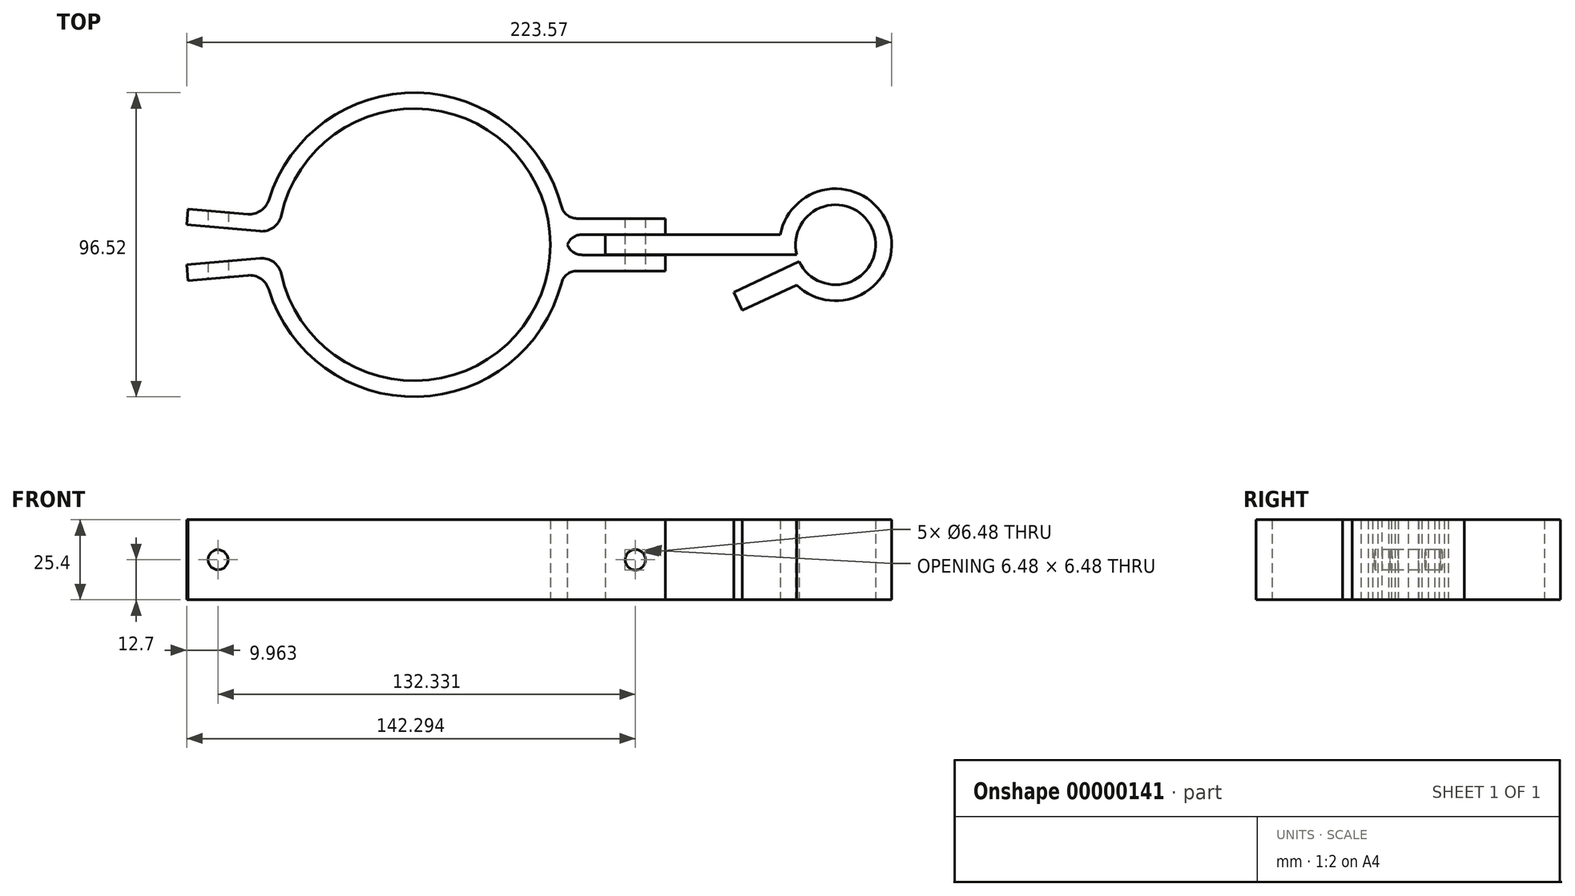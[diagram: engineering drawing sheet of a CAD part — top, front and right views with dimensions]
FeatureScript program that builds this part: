
annotation { "Feature Type Name" : "Feature", "Feature Type Description" : "" }
export const myFeature = defineFeature(function(context is Context, id is Id, definition is map)
    precondition{}
    {
        {
            var Q0;
            Q0=qCreatedBy(makeId("Top.planeOp"),FACE);
            var sketch = newSketch(context, id + "F0", { "sketchPlane" : qUnion([Q0])});
            skArc(sketch, "E0", {"start": v(-46.13, -14.18) * mm, "mid": v(48.26, 0) * mm, "end": v(-46.13, 14.18) * mm});
            skArc(sketch, "E1", {"start": v(-42.18, -9.25) * mm, "mid": v(43.18, 0) * mm, "end": v(-42.18, 9.25) * mm});
            skLineSegment(sketch, "E2", {"start": v(-52.75, 9.71) * mm, "end": v(-71.73, 11.38) * mm});
            skLineSegment(sketch, "E3", {"start": v(-71.73, 11.38) * mm, "end": v(-72.17, 6.31) * mm});
            skLineSegment(sketch, "E4", {"start": v(-72.17, 6.31) * mm, "end": v(-48.93, 4.28) * mm});
            skLineSegment(sketch, "E5", {"start": v(0, 0) * mm, "end": v(-48.26, 0) * mm, "construction": true});
            skLineSegment(sketch, "E6", {"start": v(0, 0) * mm, "end": v(0, 48.26) * mm, "construction": true});
            skLineSegment(sketch, "E7", {"start": v(47.54, 8.32) * mm, "end": v(79.65, 8.32) * mm});
            skLineSegment(sketch, "E8", {"start": v(79.65, 8.32) * mm, "end": v(79.65, 3.24) * mm});
            skLineSegment(sketch, "E9", {"start": v(79.65, 3.24) * mm, "end": v(48.15, 3.24) * mm});
            skLineSegment(sketch, "E10.0.MirrorCS", {"start": v(-72.17, -6.31) * mm, "end": v(-48.93, -4.28) * mm});
            skLineSegment(sketch, "E10.1.MirrorCS", {"start": v(-71.73, -11.38) * mm, "end": v(-72.17, -6.31) * mm});
            skLineSegment(sketch, "E10.2.MirrorCS", {"start": v(-52.75, -9.71) * mm, "end": v(-71.73, -11.38) * mm});
            skLineSegment(sketch, "E10.3.MirrorCS", {"start": v(79.65, -3.24) * mm, "end": v(48.15, -3.24) * mm});
            skLineSegment(sketch, "E10.4.MirrorCS", {"start": v(47.54, -8.32) * mm, "end": v(79.65, -8.32) * mm});
            skLineSegment(sketch, "E10.5.MirrorCS", {"start": v(79.65, -8.32) * mm, "end": v(79.65, -3.24) * mm});
            skPoint(sketch, "E11.visualSharp", {"position": v(-47.37, -9.24) * mm});
            skArc(sketch, "E11.filletArc", {"start": v(-46.13, -14.18) * mm, "mid": v(-48.65, -10.77) * mm, "end": v(-52.75, -9.71) * mm});
            skPoint(sketch, "E12.visualSharp", {"position": v(-47.37, 9.24) * mm});
            skArc(sketch, "E12.filletArc", {"start": v(-52.75, 9.71) * mm, "mid": v(-48.65, 10.77) * mm, "end": v(-46.13, 14.18) * mm});
            skPoint(sketch, "E13.visualSharp", {"position": v(-43.02, -3.76) * mm});
            skArc(sketch, "E13.filletArc", {"start": v(-42.18, -9.25) * mm, "mid": v(-44.62, -5.5) * mm, "end": v(-48.93, -4.28) * mm});
            skPoint(sketch, "E14.visualSharp", {"position": v(-43.02, 3.76) * mm});
            skArc(sketch, "E14.filletArc", {"start": v(-48.93, 4.28) * mm, "mid": v(-44.62, 5.5) * mm, "end": v(-42.18, 9.25) * mm});
            skSolve(sketch);
        }
        {
            var Q0;
            Q0=makeQuery(id+"F0.imprint","IMPRINT",FACE,{"disambiguationData":[TD([[makeQuery(id+"F0.imprint","IMPRINT",EDGE,{"derivedFrom":sQuery(id+"F0.wireOp",EDGE,"E1")}),-1.0]])]});
            var Q1;
            {var subQ1=sQuery(id+"F0.wireOp",EDGE,"E10.3.MirrorCS");Q1=makeQuery(id+"F0.imprint","IMPRINT",FACE,{"disambiguationData":[TD([[makeQuery(id+"F0.imprint","IMPRINT",EDGE,{"derivedFrom":subQ1}),1.0]])]});}
            var Q2;
            {var subQ1=sQuery(id+"F0.wireOp",EDGE,"E7");Q2=makeQuery(id+"F0.imprint","IMPRINT",FACE,{"disambiguationData":[TD([[makeQuery(id+"F0.imprint","IMPRINT",EDGE,{"derivedFrom":subQ1}),-1.0]])]});}
            extrude(context, id + "F1", {"entities" : qUnion([Q0, Q1, Q2]), "endBound" : BoundingType.SYMMETRIC, "depth" : 25.4 * mm});
        }
        {
            var Q0;
            Q0=qCreatedBy(makeId("Front.planeOp"),FACE);
            var sketch = newSketch(context, id + "F2", { "sketchPlane" : qUnion([Q0])});
            skCircle(sketch, "E15", {"center": v(-62.2, 0) * mm, "radius": 3.24 * mm});
            skCircle(sketch, "E16", {"center": v(70.12, 0) * mm, "radius": 3.24 * mm});
            skLineSegment(sketch, "E17", {"start": v(-62.2, 0) * mm, "end": v(-71.73, 0) * mm, "construction": true});
            skLineSegment(sketch, "E18", {"start": v(70.12, 0) * mm, "end": v(79.65, 0) * mm, "construction": true});
            skSolve(sketch);
        }
        {
            var Q0;
            Q0=makeQuery(id+"F1.opExtrude","SWEPT_EDGE",EDGE,{"disambiguationData":[OSD([sQuery(id+"F0.wireOp",EDGE,"E0"),sQuery(id+"F0.wireOp",EDGE,"E9")])]});
            var Q1;
            Q1=makeQuery(id+"F1.opExtrude","SWEPT_EDGE",EDGE,{"disambiguationData":[OSD([sQuery(id+"F0.wireOp",EDGE,"E0"),sQuery(id+"F0.wireOp",EDGE,"E10.3.MirrorCS")])]});
            var Q2;
            Q2=makeQuery(id+"F1.opExtrude","SWEPT_EDGE",EDGE,{"disambiguationData":[OSD([sQuery(id+"F0.wireOp",EDGE,"E0"),sQuery(id+"F0.wireOp",EDGE,"E7")])]});
            var Q3;
            Q3=makeQuery(id+"F1.opExtrude","SWEPT_EDGE",EDGE,{"disambiguationData":[OSD([sQuery(id+"F0.wireOp",EDGE,"E0"),sQuery(id+"F0.wireOp",EDGE,"E10.4.MirrorCS")])]});
            fillet(context, id + "F3", {"entities" : qUnion([Q0, Q1, Q2, Q3]), "radius" : 5.08 * mm, "tangentPropagation" : true, "allowEdgeOverflow" : false});
        }
        {
            var Q0;
            Q0=qCreatedBy(makeId("Top.planeOp"),FACE);
            var sketch = newSketch(context, id + "F4", { "sketchPlane" : qUnion([Q0])});
            skLineSegment(sketch, "E19.rect.bottom", {"start": v(60.6, -3.17) * mm, "end": v(121.33, -3.17) * mm});
            skLineSegment(sketch, "E19.rect.top", {"start": v(60.6, 3.18) * mm, "end": v(116.13, 3.18) * mm});
            skLineSegment(sketch, "E19.rect.left", {"start": v(60.6, -3.17) * mm, "end": v(60.6, 3.18) * mm});
            skPoint(sketch, "E19.rect.middle", {"position": v(90.96, 0) * mm});
            skArc(sketch, "E20", {"start": v(121.26, -12.77) * mm, "mid": v(150.55, 5.44) * mm, "end": v(116.13, 3.18) * mm});
            skArc(sketch, "E21", {"start": v(122.11, -5.37) * mm, "mid": v(145.58, 4.29) * mm, "end": v(121.33, -3.17) * mm});
            skLineSegment(sketch, "E22", {"start": v(122.11, -5.37) * mm, "end": v(101.3, -15.07) * mm});
            skLineSegment(sketch, "E23", {"start": v(101.3, -15.07) * mm, "end": v(104, -20.82) * mm});
            skLineSegment(sketch, "E24", {"start": v(104, -20.82) * mm, "end": v(121.26, -12.77) * mm});
            skPoint(sketch, "E25.orphan", {"position": v(121.33, 3.18) * mm});
            skSolve(sketch);
        }
        {
            var Q0;
            Q0=makeQuery(id+"F4.imprint","IMPRINT",FACE,{"disambiguationData":[TD([[makeQuery(id+"F4.imprint","IMPRINT",EDGE,{"derivedFrom":sQuery(id+"F4.wireOp",EDGE,"E19.rect.bottom")}),1.0]])]});
            extrude(context, id + "F5", {"entities" : qUnion([Q0]), "endBound" : BoundingType.SYMMETRIC, "depth" : 25.4 * mm});
        }
        {
            var Q0;
            {Q0=qUnion([makeQuery(id+"F2.imprint","IMPRINT",FACE,{"disambiguationData":[TD([[makeQuery(id+"F2.imprint","IMPRINT",EDGE,{"derivedFrom":sQuery(id+"F2.wireOp",EDGE,"E15")}),1.0]])]}),makeQuery(id+"F2.imprint","IMPRINT",FACE,{"disambiguationData":[TD([[makeQuery(id+"F2.imprint","IMPRINT",EDGE,{"derivedFrom":sQuery(id+"F2.wireOp",EDGE,"E16")}),1.0]])]})]);}
            extrude(context, id + "F6", {"entities" : qUnion([Q0]), "operationType" : NewBodyOperationType.REMOVE, "endBound" : BoundingType.SYMMETRIC, "oppositeDirection" : true, "depth" : 25.4 * mm});
        }
    });
